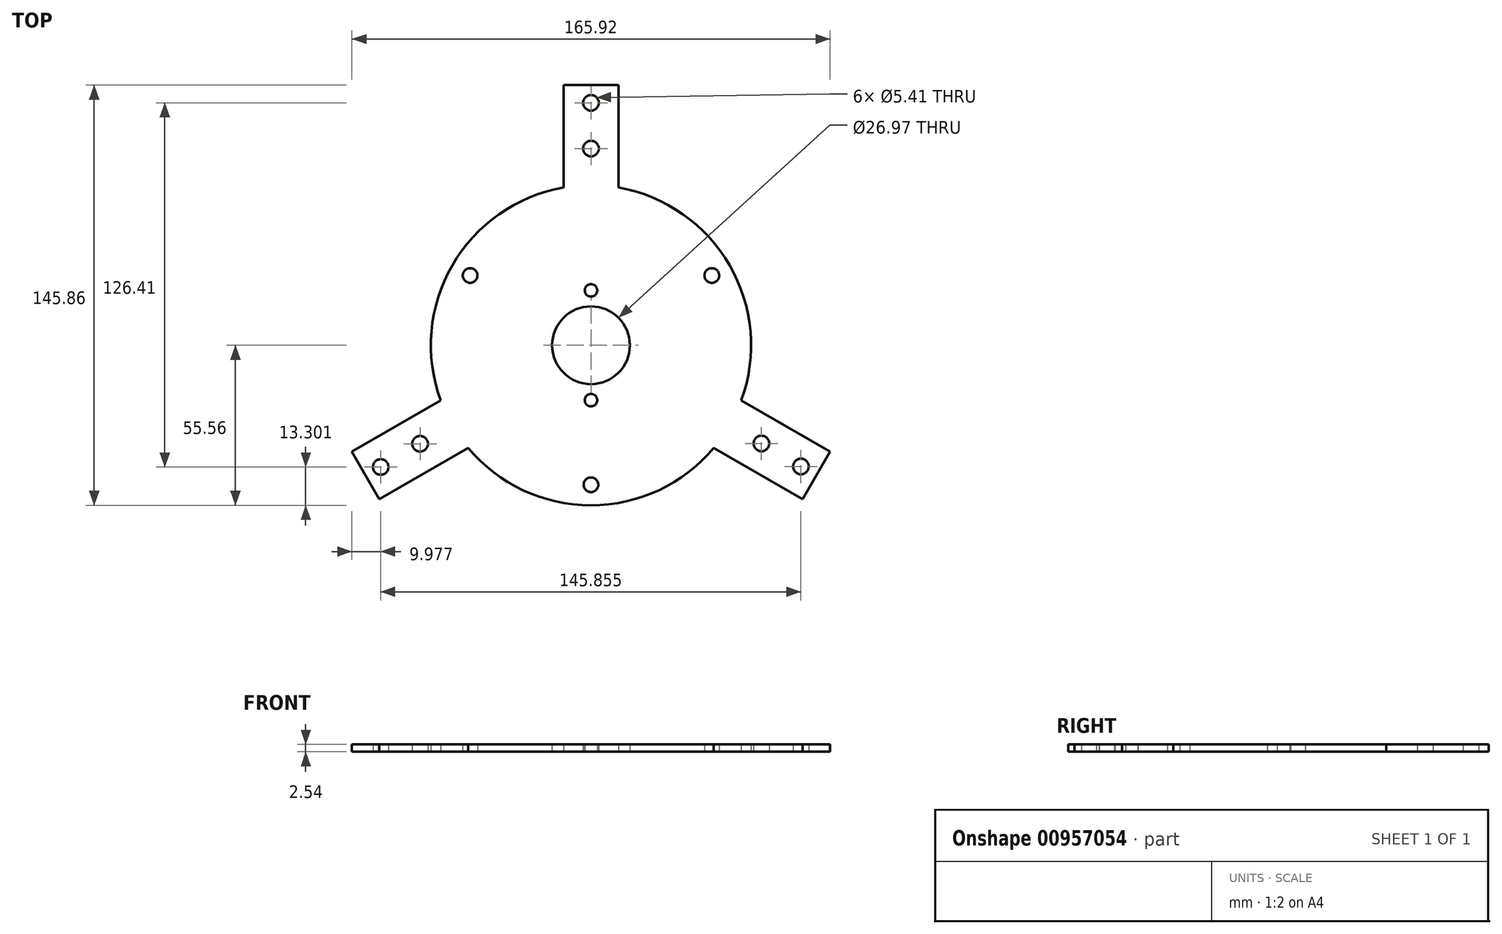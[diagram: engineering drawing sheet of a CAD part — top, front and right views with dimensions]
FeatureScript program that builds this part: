
annotation { "Feature Type Name" : "Feature", "Feature Type Description" : "" }
export const myFeature = defineFeature(function(context is Context, id is Id, definition is map)
    precondition{}
    {
        {
            var Q0;
            Q0=qCreatedBy(makeId("Top.planeOp"),FACE);
            var sketch = newSketch(context, id + "F0", { "sketchPlane" : qUnion([Q0])});
            skArc(sketch, "E0", {"start": v(-9.53, 54.74) * mm, "mid": v(-48.12, 27.78) * mm, "end": v(-52.17, -19.12) * mm});
            skLineSegment(sketch, "E1", {"start": v(-9.52, 54.74) * mm, "end": v(-9.52, 90.3) * mm});
            skLineSegment(sketch, "E2", {"start": v(-9.52, 90.3) * mm, "end": v(9.53, 90.3) * mm});
            skLineSegment(sketch, "E3", {"start": v(9.53, 90.3) * mm, "end": v(9.53, 54.74) * mm});
            skLineSegment(sketch, "E4", {"start": v(52.17, -19.12) * mm, "end": v(82.96, -36.9) * mm});
            skLineSegment(sketch, "E5", {"start": v(82.96, -36.9) * mm, "end": v(73.44, -53.4) * mm});
            skLineSegment(sketch, "E6", {"start": v(73.44, -53.4) * mm, "end": v(42.64, -35.62) * mm});
            skLineSegment(sketch, "E7", {"start": v(-42.64, -35.62) * mm, "end": v(-73.44, -53.4) * mm});
            skLineSegment(sketch, "E8", {"start": v(-73.44, -53.4) * mm, "end": v(-82.96, -36.9) * mm});
            skLineSegment(sketch, "E9", {"start": v(-82.96, -36.9) * mm, "end": v(-52.17, -19.12) * mm});
            skArc(sketch, "E10.trimOffspring", {"start": v(-42.64, -35.62) * mm, "mid": v(0, -55.56) * mm, "end": v(42.64, -35.62) * mm});
            skArc(sketch, "E11.trimOffspring", {"start": v(52.17, -19.12) * mm, "mid": v(48.12, 27.78) * mm, "end": v(9.53, 54.74) * mm});
            skCircle(sketch, "E12", {"center": v(0, 0) * mm, "radius": 13.49 * mm});
            skSolve(sketch);
        }
        {
            var Q0;
            Q0 = qSketchRegion(id + "F0", true);
            extrude(context, id + "F1", {"entities" : qUnion([Q0]), "depth" : 2.54 * mm, "offsetDistance" : 25.4 * mm});
        }
        {
            var Q0;
            Q0=qCreatedBy(makeId("Top.planeOp"),FACE);
            var sketch = newSketch(context, id + "F2", { "sketchPlane" : qUnion([Q0])});
            skCircle(sketch, "E13", {"center": v(0, 84.15) * mm, "radius": 2.7 * mm});
            skCircle(sketch, "E14", {"center": v(0, 68.28) * mm, "radius": 2.7 * mm});
            skCircle(sketch, "E15", {"center": v(72.87, -42.08) * mm, "radius": 2.7 * mm});
            skCircle(sketch, "E16", {"center": v(59.16, -34.1) * mm, "radius": 2.7 * mm});
            skCircle(sketch, "E17", {"center": v(-72.98, -42.26) * mm, "radius": 2.7 * mm});
            skCircle(sketch, "E18", {"center": v(-59.31, -34.18) * mm, "radius": 2.7 * mm});
            skSolve(sketch);
        }
        {
            var Q0;
            Q0=qCreatedBy(makeId("Top.planeOp"),FACE);
            var sketch = newSketch(context, id + "F3", { "sketchPlane" : qUnion([Q0])});
            skCircle(sketch, "E19", {"center": v(-41.94, 24.21) * mm, "radius": 2.55 * mm});
            skCircle(sketch, "E20", {"center": v(41.94, 24.21) * mm, "radius": 2.55 * mm});
            skCircle(sketch, "E21", {"center": v(0, -48.43) * mm, "radius": 2.55 * mm});
            skCircle(sketch, "E22", {"center": v(0, 19.05) * mm, "radius": 2.17 * mm});
            skCircle(sketch, "E23", {"center": v(0, -19.05) * mm, "radius": 2.17 * mm});
            skPoint(sketch, "E24.orphan", {"position": v(0, 0) * mm});
            skSolve(sketch);
        }
        {
            var Q0;
            Q0 = qSketchRegion(id + "F2", true);
            var Q1;
            Q1 = qSketchRegion(id + "F3", true);
            extrude(context, id + "F4", {"entities" : qUnion([Q0, Q1]), "operationType" : NewBodyOperationType.REMOVE, "depth" : 2.54 * mm, "offsetDistance" : 25.4 * mm});
        }
    });
